annotation { "Feature Type Name" : "Feature", "Feature Type Description" : "" }
export const myFeature = defineFeature(function(context is Context, id is Id, definition is map)
    precondition{}
    {
        {
            var Q0;
            Q0=qCreatedBy(makeId("Front.planeOp"),FACE);
            var sketch = newSketch(context, id + "F0", { "sketchPlane" : qUnion([Q0])});
            skLineSegment(sketch, "E0.bottom", {"start": v(-22.55, 4.38) * mm, "end": v(-12.23, 4.38) * mm});
            skLineSegment(sketch, "E0.top", {"start": v(-22.55, -3.36) * mm, "end": v(-12.23, -3.36) * mm});
            skLineSegment(sketch, "E0.left", {"start": v(-24.55, 2.38) * mm, "end": v(-24.55, -1.36) * mm});
            skLineSegment(sketch, "E0.right", {"start": v(-10.23, 2.38) * mm, "end": v(-10.23, -1.36) * mm});
            skPoint(sketch, "E1.visualSharp", {"position": v(-24.55, 4.38) * mm});
            skArc(sketch, "E1.filletArc", {"start": v(-22.55, 4.38) * mm, "mid": v(-23.96, 3.79) * mm, "end": v(-24.55, 2.38) * mm});
            skPoint(sketch, "E2.visualSharp", {"position": v(-24.55, -3.36) * mm});
            skArc(sketch, "E2.filletArc", {"start": v(-24.55, -1.36) * mm, "mid": v(-23.96, -2.78) * mm, "end": v(-22.55, -3.36) * mm});
            skPoint(sketch, "E3.visualSharp", {"position": v(-10.23, -3.36) * mm});
            skArc(sketch, "E3.filletArc", {"start": v(-12.23, -3.36) * mm, "mid": v(-10.81, -2.78) * mm, "end": v(-10.23, -1.36) * mm});
            skPoint(sketch, "E4.visualSharp", {"position": v(-10.23, 4.38) * mm});
            skArc(sketch, "E4.filletArc", {"start": v(-10.23, 2.38) * mm, "mid": v(-10.81, 3.79) * mm, "end": v(-12.23, 4.38) * mm});
            skText(sketch, "E5", { "text": "LUCIA CRUZ", "fontName": "OpenSans-Regular.ttf"});
            const initialGuessF0  = {"E5": [-0.02255, -0.00136, 1, 0, 0.00317]};
            skSetInitialGuess(sketch, initialGuessF0);
            skSolve(sketch);
        }
        {
            var Q0;
            Q0=makeQuery(id+"F0.imprint","IMPRINT",FACE,{"disambiguationData":[TD([[makeQuery(id+"F0.imprint","IMPRINT",EDGE,{"derivedFrom":sQuery(id+"F0.wireOp",EDGE,"E0.bottom")}),-1.0]])]});
            var sketch = newSketch(context, id + "F1", { "sketchPlane" : qUnion([Q0])});
            skSolve(sketch);
        }
        {
            var Q0;
            Q0=makeQuery(id+"F0.imprint","IMPRINT",FACE,{"disambiguationData":[TD([[makeQuery(id+"F0.imprint","IMPRINT",EDGE,{"derivedFrom":sQuery(id+"F0.wireOp",EDGE,"E0.bottom")}),-1.0]])]});
            extrude(context, id + "F2", {"entities" : qUnion([Q0]), "oppositeDirection" : true, "depth" : 0.45 * mm, "offsetDistance" : 25 * mm});
        }
        {
            var Q0;
            Q0=makeQuery(id+"F1.imprint","IMPRINT",FACE,{"disambiguationData":[TD([[makeQuery(id+"F1.imprint","IMPRINT",EDGE,{"derivedFrom":makeQuery(id+"F0.imprint","IMPRINT",EDGE,{"derivedFrom":sQuery(id+"F0.wireOp",EDGE,"E0.bottom")})}),-1.0]])]});
            extrude(context, id + "F3", {"entities" : qUnion([Q0]), "operationType" : NewBodyOperationType.ADD, "oppositeDirection" : true, "depth" : 25 * mm, "offsetDistance" : 25 * mm});
        }
    });